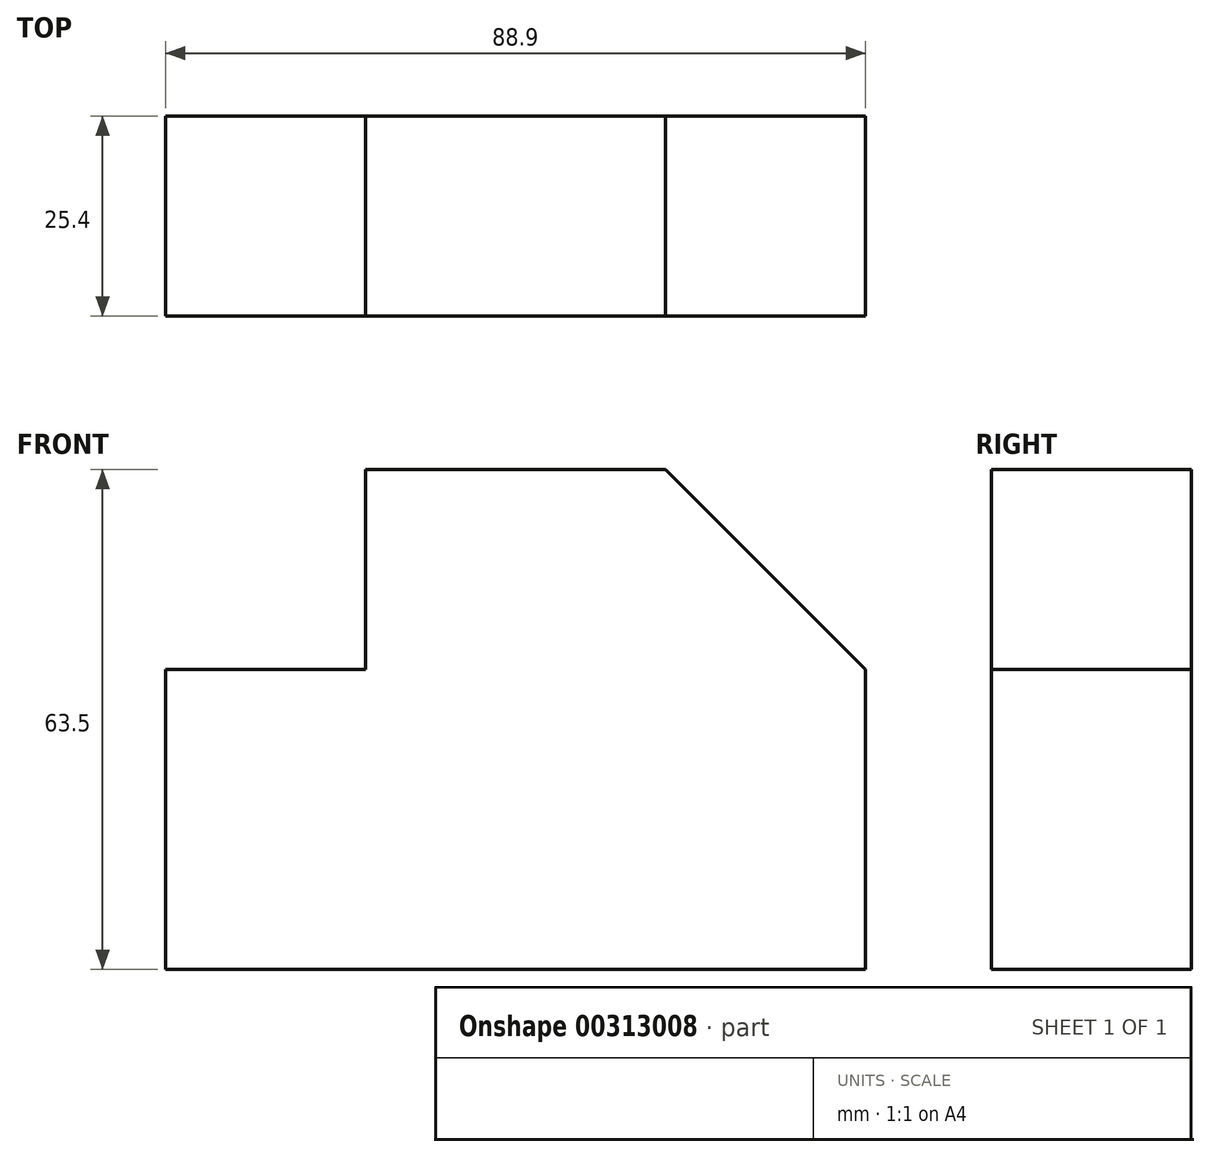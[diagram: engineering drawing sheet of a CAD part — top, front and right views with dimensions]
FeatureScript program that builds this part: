
annotation { "Feature Type Name" : "Feature", "Feature Type Description" : "" }
export const myFeature = defineFeature(function(context is Context, id is Id, definition is map)
    precondition{}
    {
        {
            var Q0;
            Q0=qCreatedBy(makeId("Front.planeOp"),FACE);
            var sketch = newSketch(context, id + "F0", { "sketchPlane" : qUnion([Q0])});
            skLineSegment(sketch, "E0", {"start": v(-29.72, -37.17) * mm, "end": v(-29.72, 0.93) * mm});
            skLineSegment(sketch, "E1", {"start": v(-29.72, 0.93) * mm, "end": v(-4.32, 0.93) * mm});
            skLineSegment(sketch, "E2", {"start": v(-4.32, 0.93) * mm, "end": v(-4.32, 26.33) * mm});
            skLineSegment(sketch, "E3", {"start": v(-4.32, 26.33) * mm, "end": v(33.78, 26.33) * mm});
            skLineSegment(sketch, "E4", {"start": v(33.78, 26.33) * mm, "end": v(59.18, 0.93) * mm});
            skLineSegment(sketch, "E5", {"start": v(59.18, 0.93) * mm, "end": v(59.18, -37.17) * mm});
            skLineSegment(sketch, "E6", {"start": v(59.18, -37.17) * mm, "end": v(-29.72, -37.17) * mm});
            skSolve(sketch);
        }
        {
            var Q0;
            Q0=makeQuery(id+"F0.imprint","IMPRINT",FACE,{"disambiguationData":[TD([[makeQuery(id+"F0.imprint","IMPRINT",EDGE,{"derivedFrom":sQuery(id+"F0.wireOp",EDGE,"E0")}),-1.0]])]});
            extrude(context, id + "F1", {"entities" : qUnion([Q0]), "depth" : 25.4 * mm});
        }
    });
